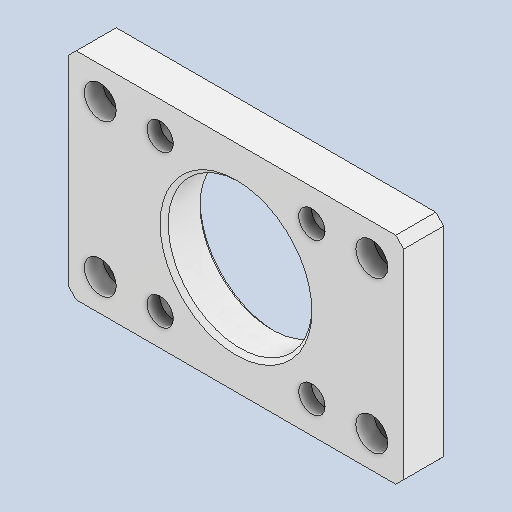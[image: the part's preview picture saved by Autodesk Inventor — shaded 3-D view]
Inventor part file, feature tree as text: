
AUTODESK INVENTOR PART (.ipt)
format: ipt  version: 2025.2 (Build 292293000, 293)  size: 155,648 bytes
history: native  units: mm
features: other x2, sketch x2
ambient origin geometry x8: Origin, YZ Plane, XZ Plane, XY Plane, X Axis, Y Axis, Z Axis, Center Point
bodies: Solid1 (feature_tree)
feature tree (4):
  other  "Sólido1"
  other  "Geometria reparada1"
  sketch  "Sketch2-Invisible"
  sketch  "Sketch1-Invisible"
